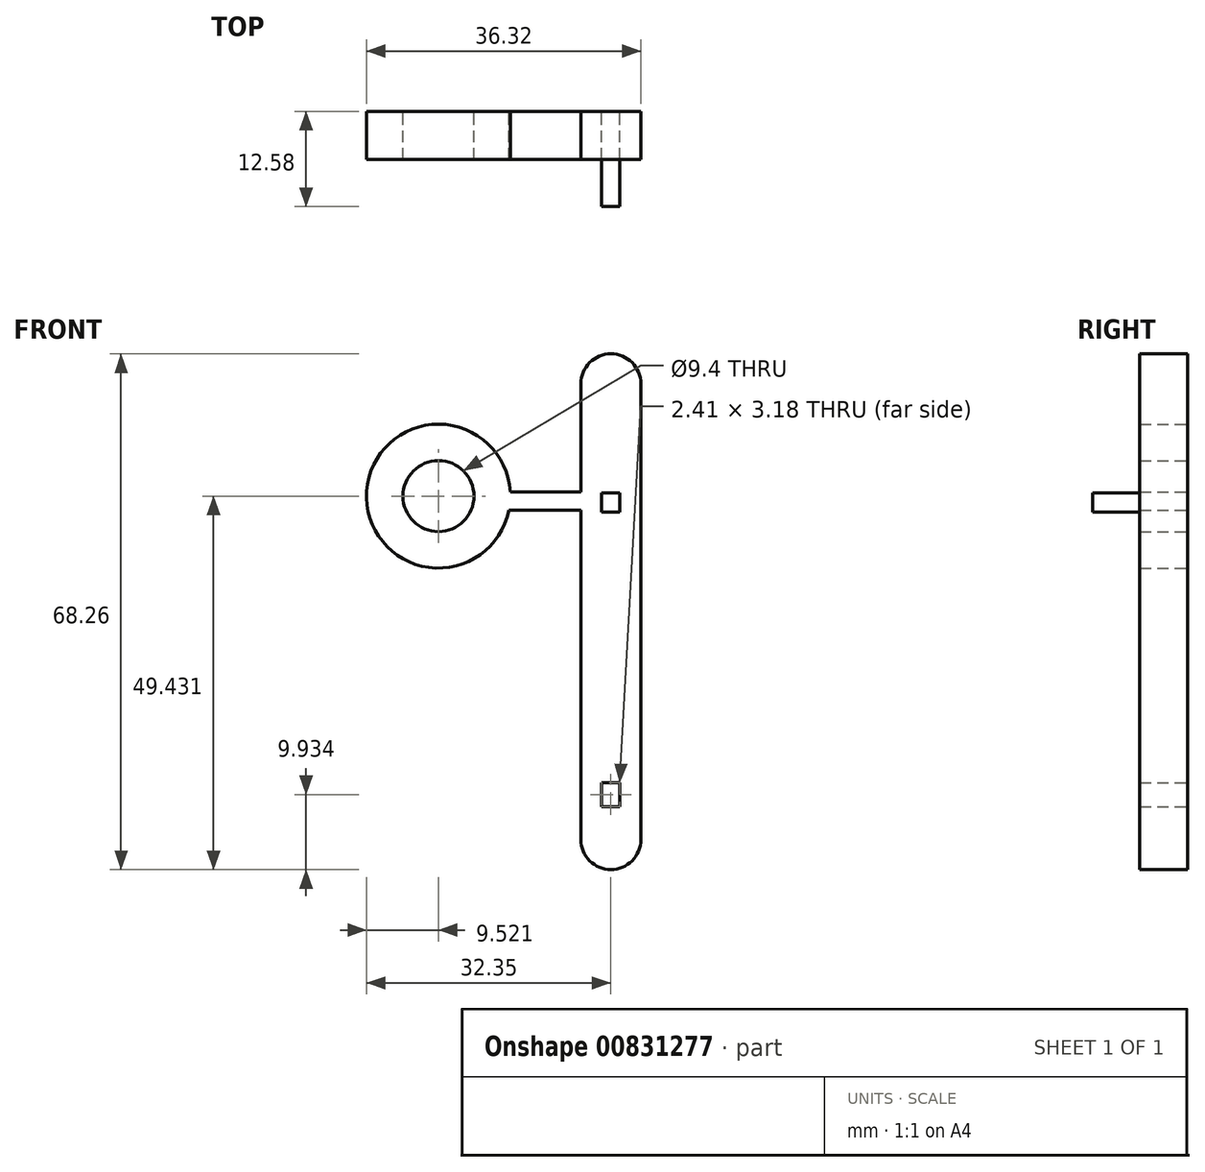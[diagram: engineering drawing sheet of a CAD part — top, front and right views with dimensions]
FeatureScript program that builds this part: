
annotation { "Feature Type Name" : "Feature", "Feature Type Description" : "" }
export const myFeature = defineFeature(function(context is Context, id is Id, definition is map)
    precondition{}
    {
        {
            var Q0;
            Q0=qCreatedBy(makeId("Front.planeOp"),FACE);
            var sketch = newSketch(context, id + "F0", { "sketchPlane" : qUnion([Q0])});
            skLineSegment(sketch, "E0.left", {"start": v(3.97, 30.16) * mm, "end": v(3.97, -30.16) * mm});
            skLineSegment(sketch, "E0.right", {"start": v(-3.97, 30.16) * mm, "end": v(-3.97, -30.16) * mm});
            skPoint(sketch, "E0.middle", {"position": v(0, 0) * mm});
            skArc(sketch, "E1", {"start": v(3.97, 30.16) * mm, "mid": v(0, 34.13) * mm, "end": v(-3.97, 30.16) * mm});
            skArc(sketch, "E2", {"start": v(-3.97, -30.16) * mm, "mid": v(0, -34.13) * mm, "end": v(3.97, -30.16) * mm});
            skLineSegment(sketch, "E3", {"start": v(-3.97, 15.87) * mm, "end": v(-13.5, 15.87) * mm});
            skLineSegment(sketch, "E4", {"start": v(-13.5, 13.41) * mm, "end": v(-3.97, 13.41) * mm});
            skCircle(sketch, "E5", {"center": v(-22.83, 15.3) * mm, "radius": 9.53 * mm});
            skCircle(sketch, "E6", {"center": v(-22.83, 15.3) * mm, "radius": 4.7 * mm});
            skLineSegment(sketch, "E7.bottom", {"start": v(-1.2, 15.75) * mm, "end": v(1.2, 15.75) * mm});
            skLineSegment(sketch, "E7.top", {"start": v(-1.2, 13.21) * mm, "end": v(1.2, 13.21) * mm});
            skLineSegment(sketch, "E7.left", {"start": v(-1.2, 15.75) * mm, "end": v(-1.2, 13.21) * mm});
            skLineSegment(sketch, "E7.right", {"start": v(1.2, 15.75) * mm, "end": v(1.2, 13.21) * mm});
            skPoint(sketch, "E7.middle", {"position": v(0, 14.48) * mm});
            skLineSegment(sketch, "E8.bottom", {"start": v(1.2, -22.6) * mm, "end": v(-1.2, -22.6) * mm});
            skLineSegment(sketch, "E8.top", {"start": v(1.2, -25.79) * mm, "end": v(-1.2, -25.79) * mm});
            skLineSegment(sketch, "E8.left", {"start": v(1.2, -22.6) * mm, "end": v(1.2, -25.79) * mm});
            skLineSegment(sketch, "E8.right", {"start": v(-1.2, -22.6) * mm, "end": v(-1.2, -25.79) * mm});
            skPoint(sketch, "E8.middle", {"position": v(0, -24.2) * mm});
            skSolve(sketch);
        }
        {
            var Q0;
            Q0=makeQuery(id+"F0.imprint","IMPRINT",FACE,{"disambiguationData":[TD([[makeQuery(id+"F0.imprint","IMPRINT",EDGE,{"derivedFrom":sQuery(id+"F0.wireOp",EDGE,"E0.bottom")}),1.0]])]});
            var Q1;
            Q1=makeQuery(id+"F0.imprint","IMPRINT",FACE,{"disambiguationData":[TD([[makeQuery(id+"F0.imprint","IMPRINT",EDGE,{"derivedFrom":sQuery(id+"F0.wireOp",EDGE,"E0.bottom")}),-1.0]])]});
            var Q2;
            Q2=makeQuery(id+"F0.imprint","IMPRINT",FACE,{"disambiguationData":[TD([[makeQuery(id+"F0.imprint","IMPRINT",EDGE,{"derivedFrom":sQuery(id+"F0.wireOp",EDGE,"E0.top")}),1.0]])]});
            var Q3;
            Q3=makeQuery(id+"F0.imprint","IMPRINT",FACE,{"disambiguationData":[TD([[makeQuery(id+"F0.imprint","IMPRINT",EDGE,{"derivedFrom":sQuery(id+"F0.wireOp",EDGE,"E5")}),1.0]])]});
            var Q4;
            {var subQ1=sQuery(id+"F0.wireOp",EDGE,"E0.bottom");Q4=makeQuery(id+"F0.imprint","IMPRINT",FACE,{"disambiguationData":[TD([[makeQuery(id+"F0.imprint","IMPRINT",EDGE,{"derivedFrom":subQ1}),1.0]])]});}
            var Q5;
            {var subQ3=sQuery(id+"F0.wireOp",EDGE,"E3");Q5=makeQuery(id+"F0.imprint","IMPRINT",FACE,{"disambiguationData":[TD([[makeQuery(id+"F0.imprint","IMPRINT",EDGE,{"derivedFrom":subQ3}),1.0]])]});}
            var Q6;
            {var subQ5=sQuery(id+"F0.wireOp",EDGE,"iJlnOxbe-qxWh-mUN0-A3kf-zTqFhj45ePgr");Q6=makeQuery(id+"F0.imprint","IMPRINT",FACE,{"disambiguationData":[TD([[makeQuery(id+"F0.imprint","IMPRINT",EDGE,{"derivedFrom":subQ5}),-1.0]])]});}
            var Q7;
            {var subQ3=sQuery(id+"F0.wireOp",EDGE,"E4");Q7=makeQuery(id+"F0.imprint","IMPRINT",FACE,{"disambiguationData":[TD([[makeQuery(id+"F0.imprint","IMPRINT",EDGE,{"derivedFrom":subQ3}),1.0]])]});}
            var Q8;
            Q8=makeQuery(id+"F0.imprint","IMPRINT",FACE,{"disambiguationData":[TD([[makeQuery(id+"F0.imprint","IMPRINT",EDGE,{"derivedFrom":sQuery(id+"F0.wireOp",EDGE,"E0.left")}),-1.0]])]});
            extrude(context, id + "F1", {"entities" : qUnion([Q0, Q1, Q2, Q3, Q4, Q5, Q6, Q7, Q8]), "endBound" : BoundingType.SYMMETRIC, "depth" : 6.35 * mm, "offsetDistance" : 25.4 * mm});
        }
        {
            var Q0;
            Q0=makeQuery(id+"F0.imprint","IMPRINT",FACE,{"disambiguationData":[TD([[makeQuery(id+"F0.imprint","IMPRINT",EDGE,{"derivedFrom":sQuery(id+"F0.wireOp",EDGE,"E7.bottom")}),-1.0]])]});
            extrude(context, id + "F2", {"entities" : qUnion([Q0]), "operationType" : NewBodyOperationType.ADD, "depth" : 9.4 * mm, "offsetDistance" : 25.4 * mm});
        }
        {
            var Q0;
            Q0=makeQuery(id+"F0.imprint","IMPRINT",FACE,{"disambiguationData":[TD([[makeQuery(id+"F0.imprint","IMPRINT",EDGE,{"derivedFrom":sQuery(id+"F0.wireOp",EDGE,"E7.bottom")}),-1.0]])]});
            extrude(context, id + "F3", {"entities" : qUnion([Q0]), "operationType" : NewBodyOperationType.ADD, "oppositeDirection" : true, "depth" : 3.17 * mm, "offsetDistance" : 25.4 * mm});
        }
    });
